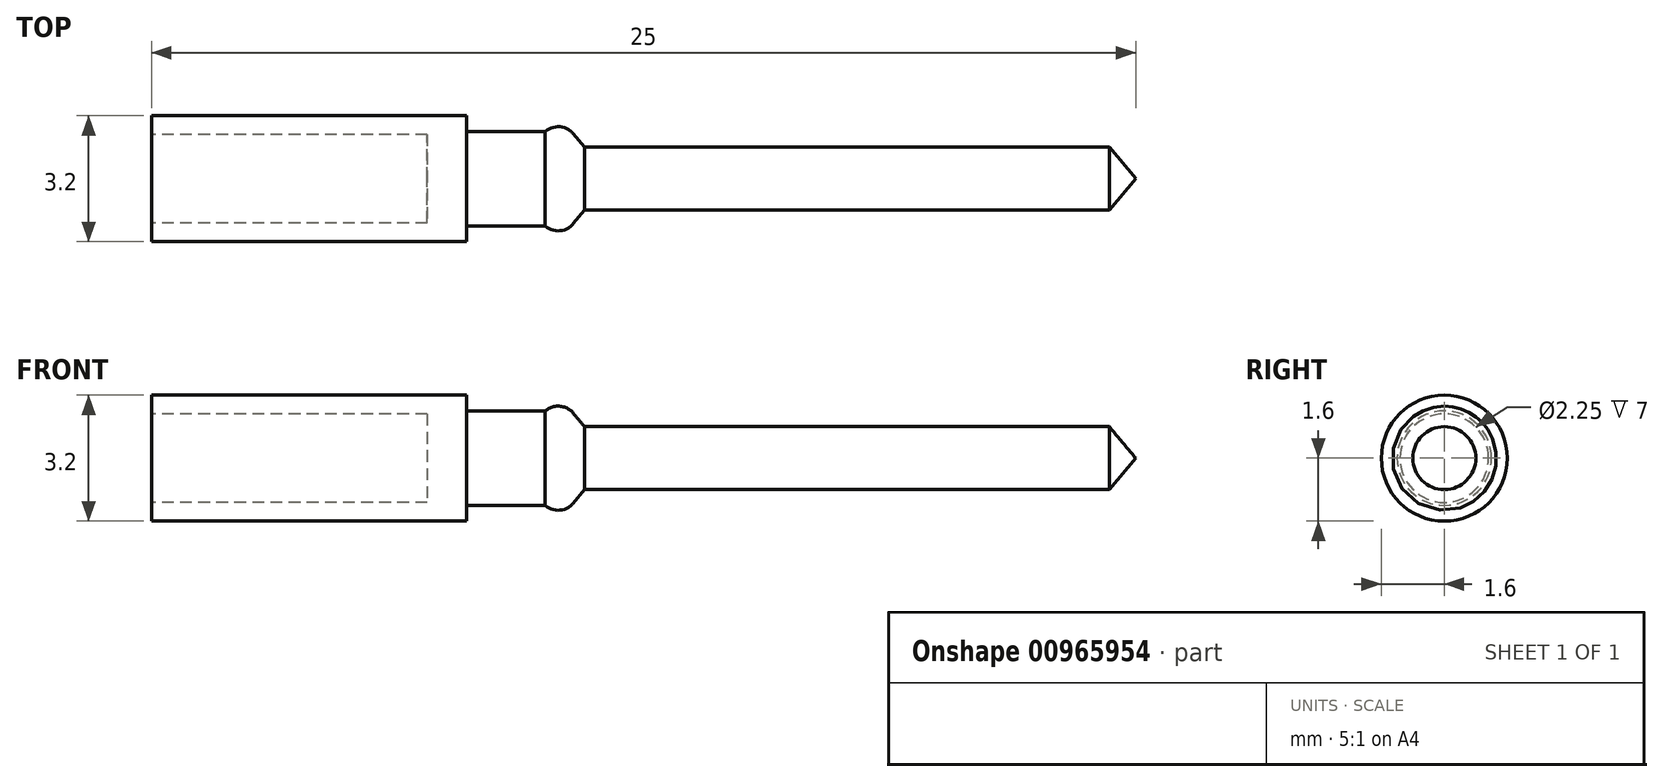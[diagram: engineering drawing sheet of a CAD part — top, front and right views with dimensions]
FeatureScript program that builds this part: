
annotation { "Feature Type Name" : "Feature", "Feature Type Description" : "" }
export const myFeature = defineFeature(function(context is Context, id is Id, definition is map)
    precondition{}
    {
        {
            var Q0;
            Q0=qCreatedBy(makeId("Top.planeOp"),FACE);
            var sketch = newSketch(context, id + "F0", { "sketchPlane" : qUnion([Q0])});
            skLineSegment(sketch, "E0", {"start": v(0, 0) * mm, "end": v(25, 0) * mm, "construction": true});
            skLineSegment(sketch, "E1", {"start": v(25, 0) * mm, "end": v(24.33, -0.8) * mm});
            skLineSegment(sketch, "E2", {"start": v(24.33, -0.8) * mm, "end": v(11, -0.8) * mm});
            skLineSegment(sketch, "E3", {"start": v(11, -0.8) * mm, "end": v(10, -2) * mm});
            skLineSegment(sketch, "E4", {"start": v(0, -1.6) * mm, "end": v(0, 0) * mm});
            skLineSegment(sketch, "E5", {"start": v(10, -2) * mm, "end": v(10, -1.2) * mm});
            skLineSegment(sketch, "E6", {"start": v(0, 0) * mm, "end": v(25, 0) * mm});
            skLineSegment(sketch, "E7", {"start": v(10, -1.2) * mm, "end": v(8, -1.2) * mm});
            skLineSegment(sketch, "E8", {"start": v(8, -1.2) * mm, "end": v(8, -1.6) * mm});
            skPoint(sketch, "E9.orphan", {"position": v(10, -1.6) * mm});
            skLineSegment(sketch, "E10", {"start": v(8, -1.6) * mm, "end": v(0, -1.6) * mm});
            skSolve(sketch);
        }
        {
            var Q0;
            Q0=makeQuery(id+"F0.imprint","IMPRINT",FACE,{"disambiguationData":[TD([[makeQuery(id+"F0.imprint","IMPRINT",EDGE,{"derivedFrom":sQuery(id+"F0.wireOp",EDGE,"E1")}),-1.0]])]});
            var Q1;
            Q1=sQuery(id+"F0.wireOp",EDGE,"E6");
            revolve(context, id + "F1", {"surfaceOperationType" : NewSurfaceOperationType.NEW, "entities" : qUnion([Q0]), "axis" : qUnion([Q1]), "revolveType" : RevolveType.FULL});
        }
        {
            var Q0;
            Q0=makeQuery(id+"F1.opRevolve","SWEPT_EDGE",EDGE,{"disambiguationData":[OSD([sQuery(id+"F0.wireOp",EDGE,"E3"),sQuery(id+"F0.wireOp",EDGE,"E5")])]});
            fillet(context, id + "F2", {"entities" : qUnion([Q0]), "radius" : .5 * mm, "tangentPropagation" : true, "allowEdgeOverflow" : false});
        }
        {
            var Q0;
            Q0=makeQuery(id+"F1.opRevolve","SWEPT_FACE",FACE,{"disambiguationData":[OSD([sQuery(id+"F0.wireOp",EDGE,"E4")])]});
            var sketch = newSketch(context, id + "F3", { "sketchPlane" : qUnion([Q0])});
            skCircle(sketch, "E11", {"center": v(0, 0) * mm, "radius": 1.13 * mm});
            skSolve(sketch);
        }
        {
            var Q0;
            Q0=makeQuery(id+"F3.imprint","IMPRINT",FACE,{"disambiguationData":[TD([[makeQuery(id+"F3.imprint","IMPRINT",EDGE,{"derivedFrom":sQuery(id+"F3.wireOp",EDGE,"E11")}),1.0]])]});
            extrude(context, id + "F4", {"entities" : qUnion([Q0]), "operationType" : NewBodyOperationType.REMOVE, "oppositeDirection" : true, "depth" : 7 * mm, "offsetDistance" : 25 * mm});
        }
    });
